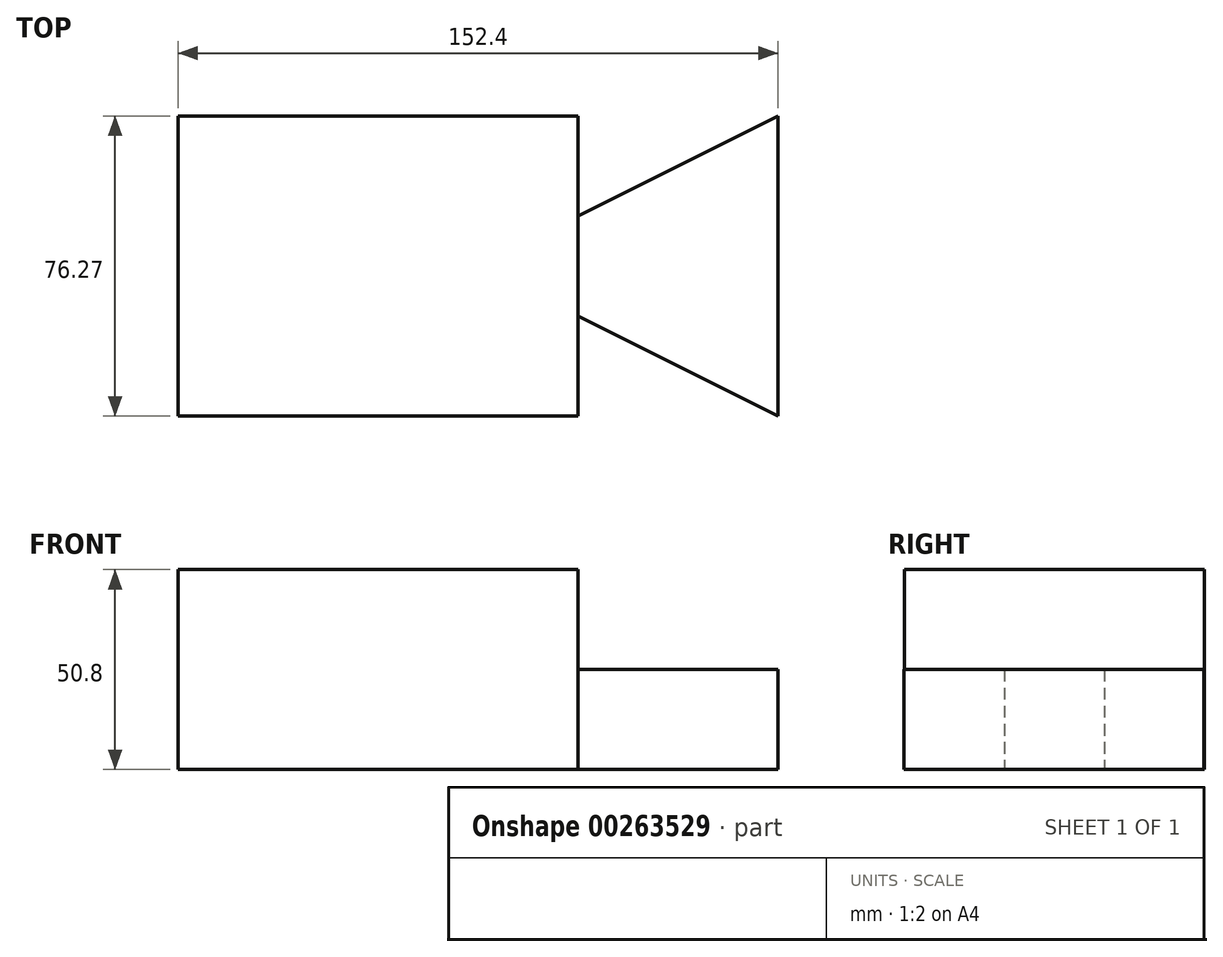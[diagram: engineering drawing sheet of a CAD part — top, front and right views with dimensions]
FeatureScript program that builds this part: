
annotation { "Feature Type Name" : "Feature", "Feature Type Description" : "" }
export const myFeature = defineFeature(function(context is Context, id is Id, definition is map)
    precondition{}
    {
        {
            var Q0;
            Q0=qCreatedBy(makeId("Top.planeOp"),FACE);
            var sketch = newSketch(context, id + "F0", { "sketchPlane" : qUnion([Q0])});
            skLineSegment(sketch, "E0.bottom", {"start": v(-72.24, 43.96) * mm, "end": v(29.36, 43.96) * mm});
            skLineSegment(sketch, "E0.top", {"start": v(-72.24, -32.24) * mm, "end": v(29.36, -32.24) * mm});
            skLineSegment(sketch, "E0.left", {"start": v(-72.24, 43.96) * mm, "end": v(-72.24, -32.24) * mm});
            skLineSegment(sketch, "E0.right", {"start": v(29.36, 43.96) * mm, "end": v(29.36, 18.56) * mm});
            skLineSegment(sketch, "E1", {"start": v(80.16, 18.5) * mm, "end": v(80.16, 43.9) * mm});
            skLineSegment(sketch, "E2", {"start": v(80.16, 43.9) * mm, "end": v(29.36, 18.56) * mm});
            skLineSegment(sketch, "E3", {"start": v(80.16, 18.5) * mm, "end": v(80.16, -32.3) * mm});
            skLineSegment(sketch, "E4", {"start": v(80.16, -32.3) * mm, "end": v(29.36, -6.84) * mm});
            skLineSegment(sketch, "E5.trimOffspring", {"start": v(29.36, -6.84) * mm, "end": v(29.36, -32.24) * mm});
            skLineSegment(sketch, "E6", {"start": v(29.36, 18.56) * mm, "end": v(29.36, -6.84) * mm});
            skSolve(sketch);
        }
        {
            var Q0;
            Q0=makeQuery(id+"F0.imprint","IMPRINT",FACE,{"disambiguationData":[TD([[makeQuery(id+"F0.imprint","IMPRINT",EDGE,{"derivedFrom":sQuery(id+"F0.wireOp",EDGE,"E0.bottom")}),-1.0]])]});
            extrude(context, id + "F1", {"entities" : qUnion([Q0]), "depth" : 50.8 * mm});
        }
        {
            var Q0;
            Q0=makeQuery(id+"F0.imprint","IMPRINT",FACE,{"disambiguationData":[TD([[makeQuery(id+"F0.imprint","IMPRINT",EDGE,{"derivedFrom":sQuery(id+"F0.wireOp",EDGE,"E1")}),1.0]])]});
            extrude(context, id + "F2", {"entities" : qUnion([Q0]), "operationType" : NewBodyOperationType.ADD, "depth" : 25.4 * mm});
        }
    });
